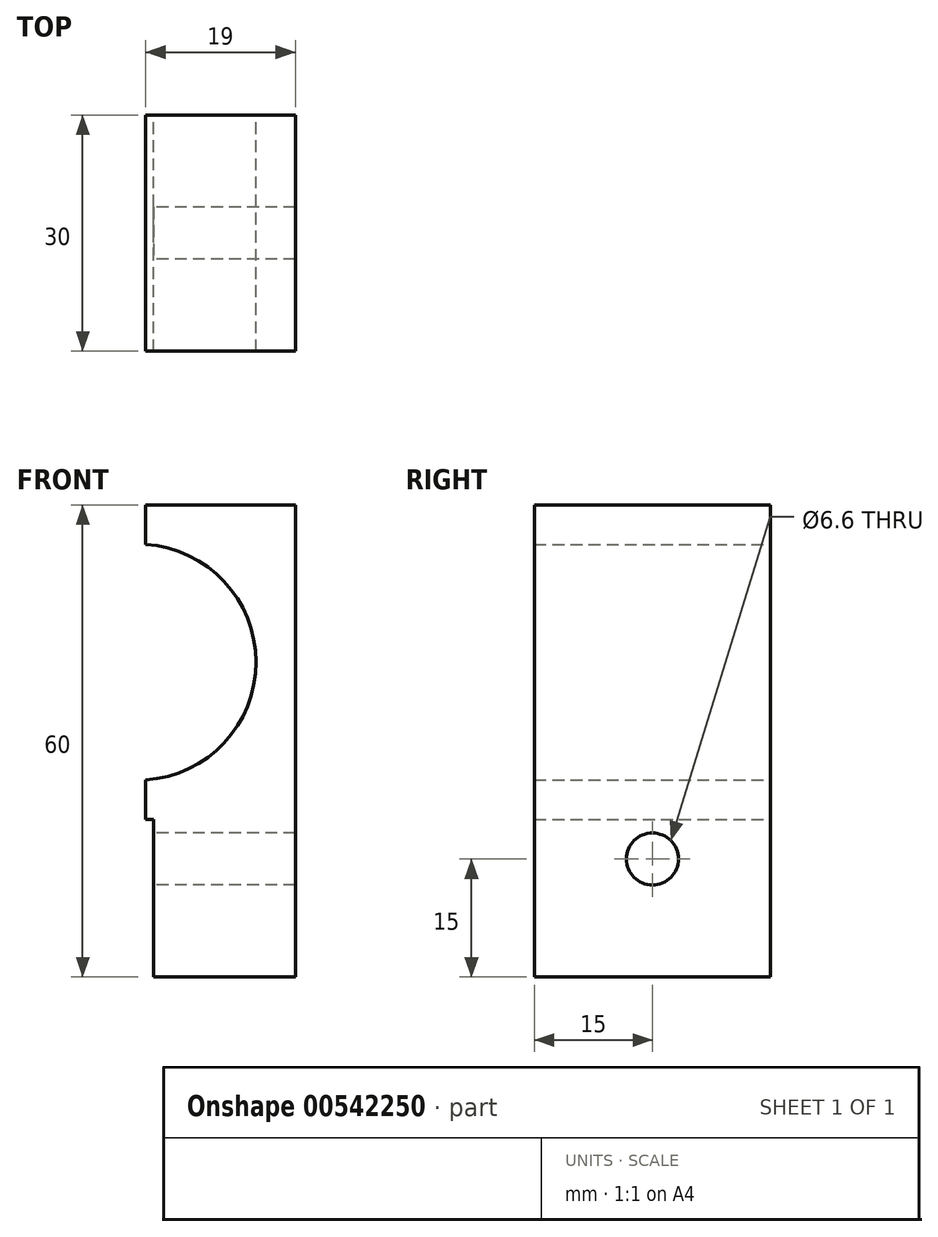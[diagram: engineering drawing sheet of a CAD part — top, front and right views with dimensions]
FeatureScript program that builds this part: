
annotation { "Feature Type Name" : "Feature", "Feature Type Description" : "" }
export const myFeature = defineFeature(function(context is Context, id is Id, definition is map)
    precondition{}
    {
        {
            var Q0;
            Q0=qCreatedBy(makeId("Front.planeOp"),FACE);
            var sketch = newSketch(context, id + "F0", { "sketchPlane" : qUnion([Q0])});
            skCircle(sketch, "E0", {"center": v(0, 0) * mm, "radius": 15 * mm});
            skLineSegment(sketch, "E1", {"start": v(1, 14.97) * mm, "end": v(1, 20) * mm});
            skLineSegment(sketch, "E2", {"start": v(1, 20) * mm, "end": v(20, 20) * mm});
            skLineSegment(sketch, "E3", {"start": v(20, 20) * mm, "end": v(20, -40) * mm});
            skLineSegment(sketch, "E4", {"start": v(20, -40) * mm, "end": v(2, -40) * mm});
            skLineSegment(sketch, "E5", {"start": v(2, -40) * mm, "end": v(2, -19.97) * mm});
            skLineSegment(sketch, "E6", {"start": v(2, -19.97) * mm, "end": v(1, -19.97) * mm});
            skLineSegment(sketch, "E7", {"start": v(1, -19.97) * mm, "end": v(1, -14.97) * mm});
            skSolve(sketch);
        }
        {
            var Q0;
            {var subQ0=sQuery(id+"F0.wireOp",EDGE,"E1");Q0=makeQuery(id+"F0.imprint","IMPRINT",FACE,{"disambiguationData":[TD([[makeQuery(id+"F0.imprint","IMPRINT",EDGE,{"derivedFrom":subQ0}),-1.0]])]});}
            extrude(context, id + "F1", {"entities" : qUnion([Q0]), "endBound" : BoundingType.SYMMETRIC, "depth" : 30 * mm, "offsetDistance" : 25 * mm});
        }
        {
            var Q0;
            Q0=qCreatedBy(makeId("Right.planeOp"),FACE);
            var sketch = newSketch(context, id + "F2", { "sketchPlane" : qUnion([Q0])});
            skPoint(sketch, "E8", {"position": v(0, -25) * mm});
            skSolve(sketch);
        }
        {
            var Q0;
            Q0=sQuery(id+"F2.wireOp",VERTEX,"E8");
            var Q1;
            Q1=makeQuery(id+"F1.opExtrude","SWEPT_BODY",BODY,{"disambiguationData":[OSD([sQuery(id+"F0.wireOp",EDGE,"E0"),sQuery(id+"F0.wireOp",EDGE,"E1"),sQuery(id+"F0.wireOp",EDGE,"E2"),sQuery(id+"F0.wireOp",EDGE,"E3"),sQuery(id+"F0.wireOp",EDGE,"E4"),sQuery(id+"F0.wireOp",EDGE,"E5"),sQuery(id+"F0.wireOp",EDGE,"E6"),sQuery(id+"F0.wireOp",EDGE,"E7")])]});
            hole(context, id + "F3", {"style" : HoleStyle.SIMPLE, "endStyle" : HoleEndStyle.THROUGH, "oppositeDirection" : true, "standardTappedOrClearance" : lookupTablePath({ "standard" : "ISO", "fit" : "Normal", "size" : "M6", "type" : "Clearance" }), "standardBlindInLast" : lookupTablePath({ "fit" : "Standard", "standard" : "ISO", "size" : "M6", "type" : "Clearance" }), "holeDiameter" : 6.6 * mm, "tappedDepth" : 12 * mm, "tapClearance" : 3, "startFromSketch" : true, "locations" : qUnion([Q0]), "scope" : qUnion([Q1])});
        }
    });
